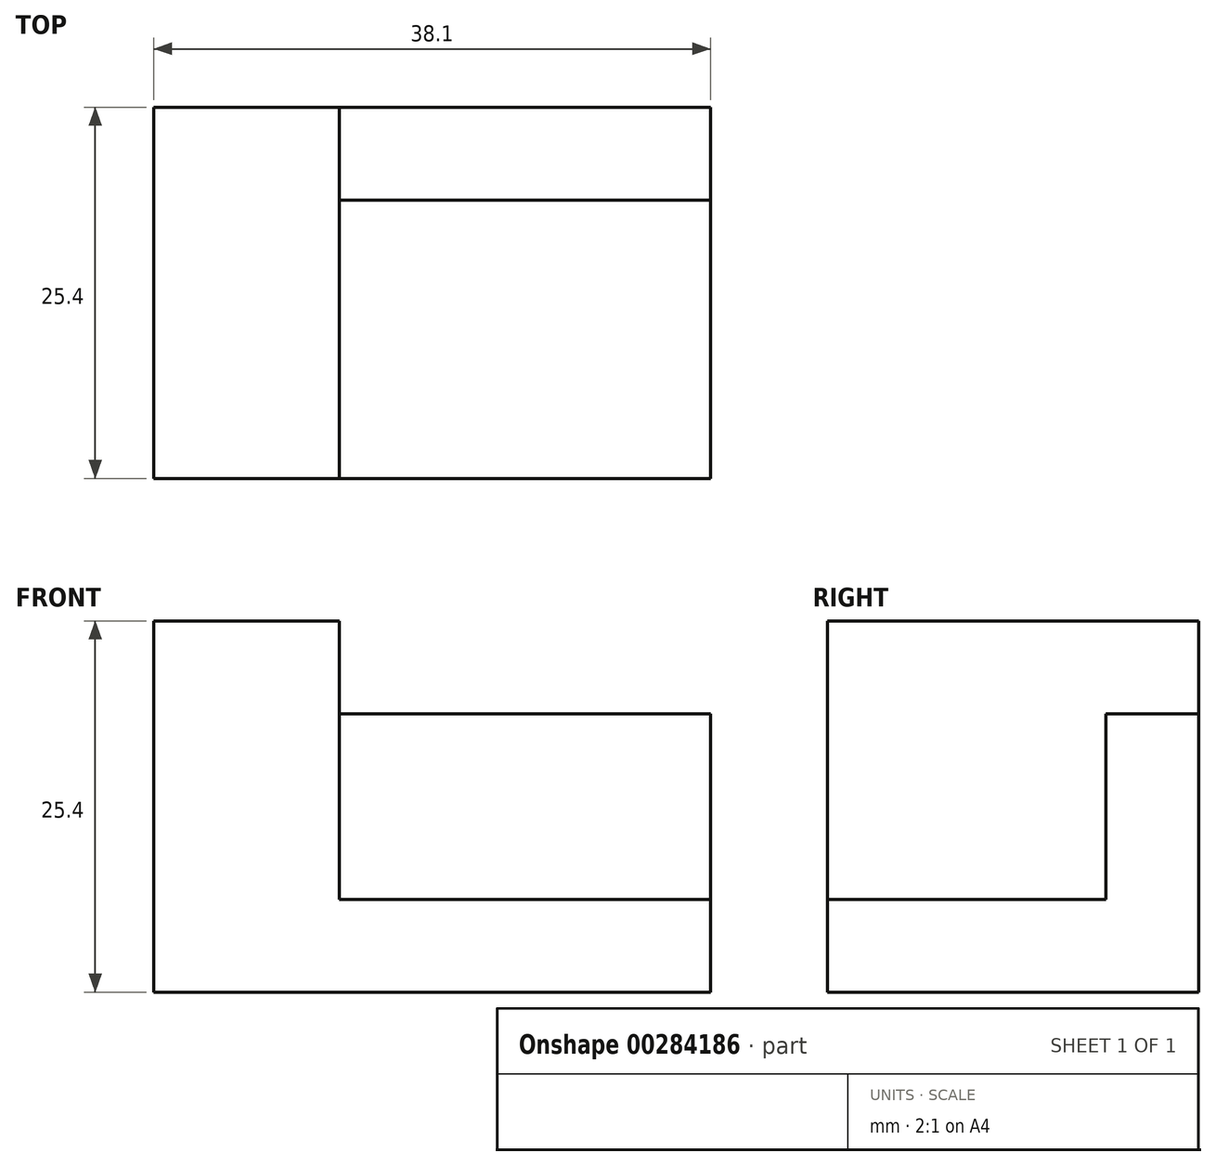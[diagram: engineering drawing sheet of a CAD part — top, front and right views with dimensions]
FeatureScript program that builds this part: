
annotation { "Feature Type Name" : "Feature", "Feature Type Description" : "" }
export const myFeature = defineFeature(function(context is Context, id is Id, definition is map)
    precondition{}
    {
        {
            var Q0;
            Q0=qCreatedBy(makeId("Front.planeOp"),FACE);
            var sketch = newSketch(context, id + "F0", { "sketchPlane" : qUnion([Q0])});
            skLineSegment(sketch, "E0", {"start": v(0, 0) * mm, "end": v(0, 25.4) * mm});
            skLineSegment(sketch, "E1", {"start": v(0, 25.4) * mm, "end": v(12.7, 25.4) * mm});
            skLineSegment(sketch, "E2", {"start": v(12.7, 25.4) * mm, "end": v(12.7, 6.35) * mm});
            skLineSegment(sketch, "E3", {"start": v(12.7, 6.35) * mm, "end": v(38.1, 6.35) * mm});
            skLineSegment(sketch, "E4", {"start": v(38.1, 6.35) * mm, "end": v(38.1, 0) * mm});
            skLineSegment(sketch, "E5", {"start": v(38.1, 0) * mm, "end": v(0, 0) * mm});
            skSolve(sketch);
        }
        {
            var Q0;
            Q0 = qSketchRegion(id + "F0", true);
            extrude(context, id + "F1", {"entities" : qUnion([Q0]), "depth" : 25.4 * mm});
        }
        {
            var Q0;
            Q0=makeQuery(id+"F1.opExtrude","SWEPT_FACE",FACE,{"disambiguationData":[OSD([sQuery(id+"F0.wireOp",EDGE,"E2")])]});
            var sketch = newSketch(context, id + "F2", { "sketchPlane" : qUnion([Q0])});
            skLineSegment(sketch, "E6.bottom", {"start": v(0, 6.35) * mm, "end": v(-6.35, 6.35) * mm});
            skLineSegment(sketch, "E6.top", {"start": v(0, 19.05) * mm, "end": v(-6.35, 19.05) * mm});
            skLineSegment(sketch, "E6.left", {"start": v(0, 6.35) * mm, "end": v(0, 19.05) * mm});
            skLineSegment(sketch, "E6.right", {"start": v(-6.35, 6.35) * mm, "end": v(-6.35, 19.05) * mm});
            skSolve(sketch);
        }
        {
            var Q0;
            Q0 = qSketchRegion(id + "F2", true);
            extrude(context, id + "F3", {"entities" : qUnion([Q0]), "operationType" : NewBodyOperationType.ADD, "depth" : 25.4 * mm});
        }
    });
